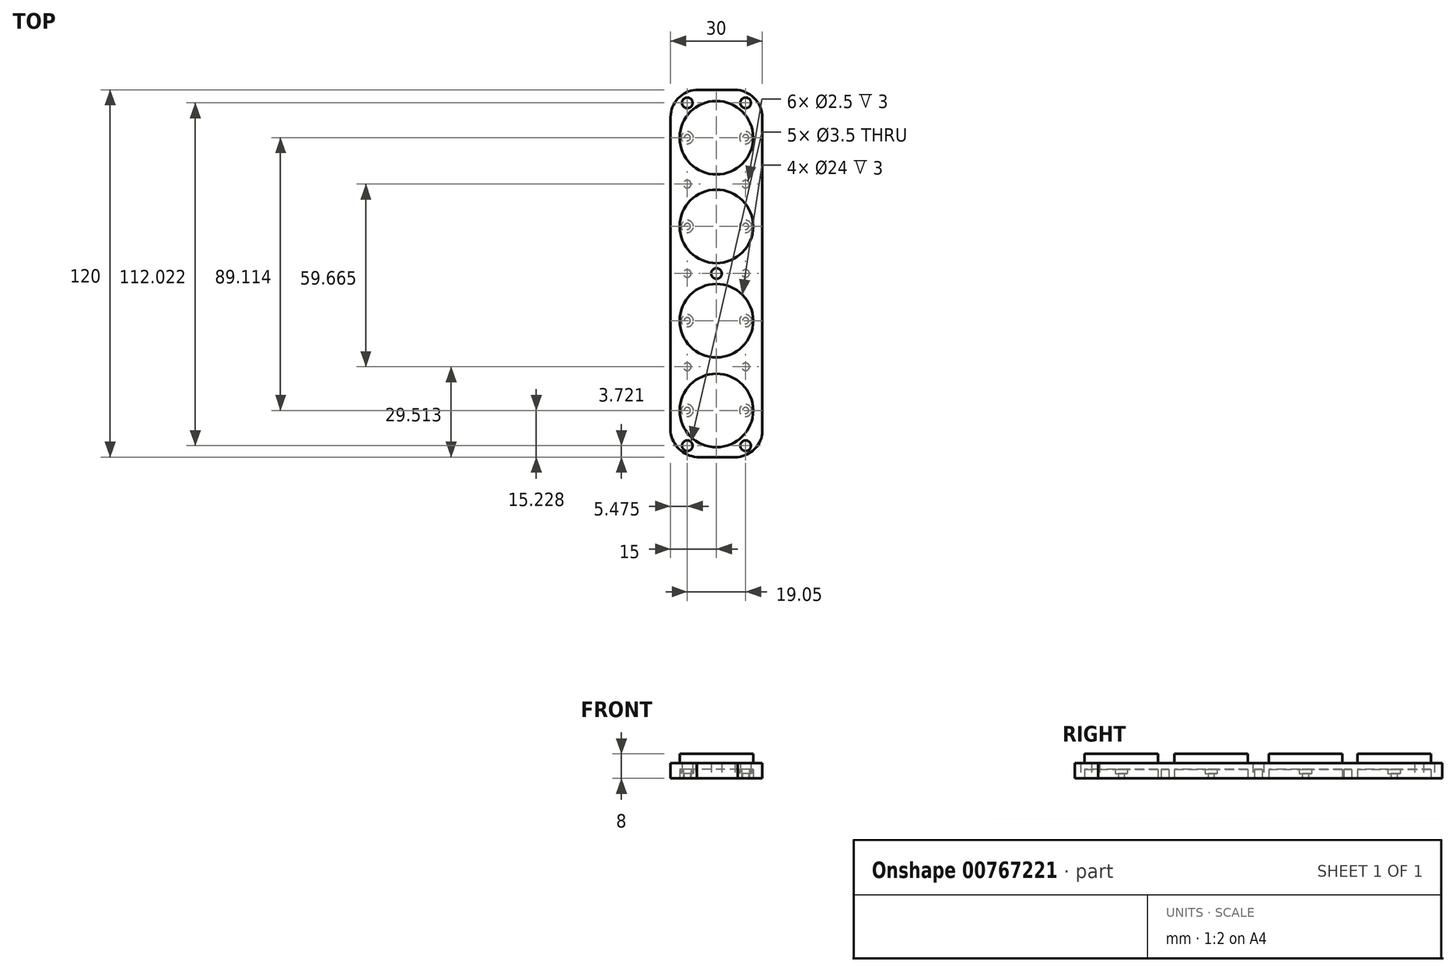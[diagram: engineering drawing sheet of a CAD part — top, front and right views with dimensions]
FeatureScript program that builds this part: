
annotation { "Feature Type Name" : "Feature", "Feature Type Description" : "" }
export const myFeature = defineFeature(function(context is Context, id is Id, definition is map)
    precondition{}
    {
        {
            var Q0;
            Q0=qCreatedBy(makeId("Top.planeOp"),FACE);
            var sketch = newSketch(context, id + "F0", { "sketchPlane" : qUnion([Q0])});
            skLineSegment(sketch, "E0.bottom", {"start": v(-15, 60.02) * mm, "end": v(15, 60.02) * mm});
            skLineSegment(sketch, "E0.top", {"start": v(-15, -59.98) * mm, "end": v(15, -59.98) * mm});
            skLineSegment(sketch, "E0.left", {"start": v(-15, 60.02) * mm, "end": v(-15, -59.98) * mm});
            skLineSegment(sketch, "E0.right", {"start": v(15, 60.02) * mm, "end": v(15, -59.98) * mm});
            skCircle(sketch, "E1", {"center": v(0, 44.36) * mm, "radius": 12 * mm});
            skCircle(sketch, "E2", {"center": v(0, 15.4) * mm, "radius": 12 * mm});
            skCircle(sketch, "E3", {"center": v(0, -15.42) * mm, "radius": 12 * mm});
            skCircle(sketch, "E4", {"center": v(0, -44.75) * mm, "radius": 12 * mm});
            skArc(sketch, "E5", {"start": v(-15, -49.5) * mm, "mid": v(-12.48, -57.1) * mm, "end": v(-5, -59.98) * mm});
            skArc(sketch, "E6", {"start": v(5, -59.98) * mm, "mid": v(12.6, -57.22) * mm, "end": v(15, -49.5) * mm});
            skArc(sketch, "E7", {"start": v(15, 50.8) * mm, "mid": v(12.4, 57.26) * mm, "end": v(6, 60.02) * mm});
            skArc(sketch, "E8", {"start": v(-5, 60.02) * mm, "mid": v(-12.07, 57.65) * mm, "end": v(-15, 50.8) * mm});
            skLineSegment(sketch, "E9", {"start": v(9.53, 68.25) * mm, "end": v(9.53, -73.05) * mm, "construction": true});
            skLineSegment(sketch, "E10", {"start": v(-9.53, 68.25) * mm, "end": v(-9.53, -73.05) * mm, "construction": true});
            skCircle(sketch, "E11", {"center": v(-9.53, 44.36) * mm, "radius": 1 * mm});
            skCircle(sketch, "E12", {"center": v(9.53, 44.36) * mm, "radius": 1 * mm});
            skCircle(sketch, "E13", {"center": v(9.53, 44.36) * mm, "radius": 2 * mm});
            skCircle(sketch, "E14", {"center": v(-9.53, 44.36) * mm, "radius": 2 * mm});
            skCircle(sketch, "E15", {"center": v(9.53, 15.4) * mm, "radius": 1 * mm});
            skCircle(sketch, "E16", {"center": v(9.53, 15.4) * mm, "radius": 2 * mm});
            skCircle(sketch, "E17", {"center": v(-9.53, 15.4) * mm, "radius": 1 * mm});
            skCircle(sketch, "E18", {"center": v(-9.53, 15.4) * mm, "radius": 2 * mm});
            skCircle(sketch, "E19", {"center": v(9.53, -15.42) * mm, "radius": 1 * mm});
            skCircle(sketch, "E20", {"center": v(9.53, -15.42) * mm, "radius": 2 * mm});
            skCircle(sketch, "E21", {"center": v(-9.53, -15.42) * mm, "radius": 1 * mm});
            skCircle(sketch, "E22", {"center": v(-9.53, -15.42) * mm, "radius": 2 * mm});
            skCircle(sketch, "E23", {"center": v(9.53, -44.75) * mm, "radius": 1 * mm});
            skCircle(sketch, "E24", {"center": v(9.53, -44.75) * mm, "radius": 2 * mm});
            skCircle(sketch, "E25", {"center": v(-9.53, -44.75) * mm, "radius": 1 * mm});
            skCircle(sketch, "E26", {"center": v(-9.53, -44.75) * mm, "radius": 2 * mm});
            skCircle(sketch, "E27", {"center": v(9.53, 55.76) * mm, "radius": 1.75 * mm});
            skCircle(sketch, "E28", {"center": v(-9.53, 55.76) * mm, "radius": 1.75 * mm});
            skCircle(sketch, "E29", {"center": v(9.53, 29.2) * mm, "radius": 1.25 * mm});
            skCircle(sketch, "E30", {"center": v(-9.53, 29.2) * mm, "radius": 1.25 * mm});
            skCircle(sketch, "E31", {"center": v(9.53, 0) * mm, "radius": 1.25 * mm});
            skCircle(sketch, "E32", {"center": v(-9.53, 0) * mm, "radius": 1.25 * mm});
            skCircle(sketch, "E33", {"center": v(9.53, -30.47) * mm, "radius": 1.25 * mm});
            skCircle(sketch, "E34", {"center": v(-9.53, -30.47) * mm, "radius": 1.25 * mm});
            skCircle(sketch, "E35", {"center": v(9.53, -56.26) * mm, "radius": 1.75 * mm});
            skCircle(sketch, "E36", {"center": v(-9.53, -56.26) * mm, "radius": 1.75 * mm});
            skCircle(sketch, "E37", {"center": v(0, 0) * mm, "radius": 1.75 * mm});
            skSolve(sketch);
        }
        {
            var Q0;
            Q0=makeQuery(id+"F0.imprint","IMPRINT",FACE,{"disambiguationData":[TD([[makeQuery(id+"F0.imprint","IMPRINT",EDGE,{"derivedFrom":sQuery(id+"F0.wireOp",EDGE,"E1")}),-1.0]])]});
            extrude(context, id + "F1", {"entities" : qUnion([Q0]), "depth" : 5 * mm, "offsetDistance" : 25 * mm});
        }
        {
            var Q0;
            Q0=makeQuery(id+"F0.imprint","IMPRINT",FACE,{"disambiguationData":[TD([[makeQuery(id+"F0.imprint","IMPRINT",EDGE,{"derivedFrom":sQuery(id+"F0.wireOp",EDGE,"E1")}),1.0]])]});
            var Q1;
            Q1=makeQuery(id+"F0.imprint","IMPRINT",FACE,{"disambiguationData":[TD([[makeQuery(id+"F0.imprint","IMPRINT",EDGE,{"derivedFrom":sQuery(id+"F0.wireOp",EDGE,"E2")}),1.0]])]});
            var Q2;
            Q2=makeQuery(id+"F0.imprint","IMPRINT",FACE,{"disambiguationData":[TD([[makeQuery(id+"F0.imprint","IMPRINT",EDGE,{"derivedFrom":sQuery(id+"F0.wireOp",EDGE,"E3")}),1.0]])]});
            var Q3;
            Q3=makeQuery(id+"F0.imprint","IMPRINT",FACE,{"disambiguationData":[TD([[makeQuery(id+"F0.imprint","IMPRINT",EDGE,{"derivedFrom":sQuery(id+"F0.wireOp",EDGE,"E4")}),1.0]])]});
            var Q4;
            Q4=makeQuery(id+"F0.imprint","IMPRINT",FACE,{"disambiguationData":[TD([[makeQuery(id+"F0.imprint","IMPRINT",EDGE,{"derivedFrom":sQuery(id+"F0.wireOp",EDGE,"E12")}),1.0]])]});
            var Q5;
            Q5=makeQuery(id+"F0.imprint","IMPRINT",FACE,{"disambiguationData":[TD([[makeQuery(id+"F0.imprint","IMPRINT",EDGE,{"derivedFrom":sQuery(id+"F0.wireOp",EDGE,"E12")}),-1.0]])]});
            var Q6;
            Q6=makeQuery(id+"F0.imprint","IMPRINT",FACE,{"disambiguationData":[TD([[makeQuery(id+"F0.imprint","IMPRINT",EDGE,{"derivedFrom":sQuery(id+"F0.wireOp",EDGE,"E11")}),1.0]])]});
            var Q7;
            Q7=makeQuery(id+"F0.imprint","IMPRINT",FACE,{"disambiguationData":[TD([[makeQuery(id+"F0.imprint","IMPRINT",EDGE,{"derivedFrom":sQuery(id+"F0.wireOp",EDGE,"E11")}),-1.0]])]});
            var Q8;
            Q8=makeQuery(id+"F0.imprint","IMPRINT",FACE,{"disambiguationData":[TD([[makeQuery(id+"F0.imprint","IMPRINT",EDGE,{"derivedFrom":sQuery(id+"F0.wireOp",EDGE,"E15")}),1.0]])]});
            var Q9;
            Q9=makeQuery(id+"F0.imprint","IMPRINT",FACE,{"disambiguationData":[TD([[makeQuery(id+"F0.imprint","IMPRINT",EDGE,{"derivedFrom":sQuery(id+"F0.wireOp",EDGE,"E15")}),-1.0]])]});
            var Q10;
            Q10=makeQuery(id+"F0.imprint","IMPRINT",FACE,{"disambiguationData":[TD([[makeQuery(id+"F0.imprint","IMPRINT",EDGE,{"derivedFrom":sQuery(id+"F0.wireOp",EDGE,"E17")}),1.0]])]});
            var Q11;
            Q11=makeQuery(id+"F0.imprint","IMPRINT",FACE,{"disambiguationData":[TD([[makeQuery(id+"F0.imprint","IMPRINT",EDGE,{"derivedFrom":sQuery(id+"F0.wireOp",EDGE,"E17")}),-1.0]])]});
            var Q12;
            Q12=makeQuery(id+"F0.imprint","IMPRINT",FACE,{"disambiguationData":[TD([[makeQuery(id+"F0.imprint","IMPRINT",EDGE,{"derivedFrom":sQuery(id+"F0.wireOp",EDGE,"E19")}),1.0]])]});
            var Q13;
            Q13=makeQuery(id+"F0.imprint","IMPRINT",FACE,{"disambiguationData":[TD([[makeQuery(id+"F0.imprint","IMPRINT",EDGE,{"derivedFrom":sQuery(id+"F0.wireOp",EDGE,"E19")}),-1.0]])]});
            var Q14;
            Q14=makeQuery(id+"F0.imprint","IMPRINT",FACE,{"disambiguationData":[TD([[makeQuery(id+"F0.imprint","IMPRINT",EDGE,{"derivedFrom":sQuery(id+"F0.wireOp",EDGE,"E21")}),1.0]])]});
            var Q15;
            Q15=makeQuery(id+"F0.imprint","IMPRINT",FACE,{"disambiguationData":[TD([[makeQuery(id+"F0.imprint","IMPRINT",EDGE,{"derivedFrom":sQuery(id+"F0.wireOp",EDGE,"E21")}),-1.0]])]});
            var Q16;
            Q16=makeQuery(id+"F0.imprint","IMPRINT",FACE,{"disambiguationData":[TD([[makeQuery(id+"F0.imprint","IMPRINT",EDGE,{"derivedFrom":sQuery(id+"F0.wireOp",EDGE,"E23")}),1.0]])]});
            var Q17;
            Q17=makeQuery(id+"F0.imprint","IMPRINT",FACE,{"disambiguationData":[TD([[makeQuery(id+"F0.imprint","IMPRINT",EDGE,{"derivedFrom":sQuery(id+"F0.wireOp",EDGE,"E23")}),-1.0]])]});
            var Q18;
            Q18=makeQuery(id+"F0.imprint","IMPRINT",FACE,{"disambiguationData":[TD([[makeQuery(id+"F0.imprint","IMPRINT",EDGE,{"derivedFrom":sQuery(id+"F0.wireOp",EDGE,"E25")}),-1.0]])]});
            var Q19;
            Q19=makeQuery(id+"F0.imprint","IMPRINT",FACE,{"disambiguationData":[TD([[makeQuery(id+"F0.imprint","IMPRINT",EDGE,{"derivedFrom":sQuery(id+"F0.wireOp",EDGE,"E25")}),1.0]])]});
            var Q20;
            Q20=makeQuery(id+"F0.imprint","IMPRINT",FACE,{"disambiguationData":[TD([[makeQuery(id+"F0.imprint","IMPRINT",EDGE,{"derivedFrom":sQuery(id+"F0.wireOp",EDGE,"E34")}),1.0]])]});
            var Q21;
            Q21=makeQuery(id+"F0.imprint","IMPRINT",FACE,{"disambiguationData":[TD([[makeQuery(id+"F0.imprint","IMPRINT",EDGE,{"derivedFrom":sQuery(id+"F0.wireOp",EDGE,"E33")}),1.0]])]});
            var Q22;
            Q22=makeQuery(id+"F0.imprint","IMPRINT",FACE,{"disambiguationData":[TD([[makeQuery(id+"F0.imprint","IMPRINT",EDGE,{"derivedFrom":sQuery(id+"F0.wireOp",EDGE,"E31")}),1.0]])]});
            var Q23;
            Q23=makeQuery(id+"F0.imprint","IMPRINT",FACE,{"disambiguationData":[TD([[makeQuery(id+"F0.imprint","IMPRINT",EDGE,{"derivedFrom":sQuery(id+"F0.wireOp",EDGE,"E32")}),1.0]])]});
            var Q24;
            Q24=makeQuery(id+"F0.imprint","IMPRINT",FACE,{"disambiguationData":[TD([[makeQuery(id+"F0.imprint","IMPRINT",EDGE,{"derivedFrom":sQuery(id+"F0.wireOp",EDGE,"E30")}),1.0]])]});
            var Q25;
            Q25=makeQuery(id+"F0.imprint","IMPRINT",FACE,{"disambiguationData":[TD([[makeQuery(id+"F0.imprint","IMPRINT",EDGE,{"derivedFrom":sQuery(id+"F0.wireOp",EDGE,"E29")}),1.0]])]});
            extrude(context, id + "F2", {"entities" : qUnion([Q0, Q1, Q2, Q3, Q4, Q5, Q6, Q7, Q8, Q9, Q10, Q11, Q12, Q13, Q14, Q15, Q16, Q17, Q18, Q19, Q20, Q21, Q22, Q23, Q24, Q25]), "operationType" : NewBodyOperationType.ADD, "depth" : 5 * mm, "offsetDistance" : 25 * mm, "hasSecondDirection" : true, "secondDirectionOppositeDirection" : false, "secondDirectionDepth" : 3 * mm});
        }
        {
            var Q0;
            Q0=makeQuery(id+"F0.imprint","IMPRINT",FACE,{"disambiguationData":[TD([[makeQuery(id+"F0.imprint","IMPRINT",EDGE,{"derivedFrom":sQuery(id+"F0.wireOp",EDGE,"E12")}),1.0]])]});
            var Q1;
            Q1=makeQuery(id+"F0.imprint","IMPRINT",FACE,{"disambiguationData":[TD([[makeQuery(id+"F0.imprint","IMPRINT",EDGE,{"derivedFrom":sQuery(id+"F0.wireOp",EDGE,"E11")}),1.0]])]});
            var Q2;
            Q2=makeQuery(id+"F0.imprint","IMPRINT",FACE,{"disambiguationData":[TD([[makeQuery(id+"F0.imprint","IMPRINT",EDGE,{"derivedFrom":sQuery(id+"F0.wireOp",EDGE,"E15")}),1.0]])]});
            var Q3;
            Q3=makeQuery(id+"F0.imprint","IMPRINT",FACE,{"disambiguationData":[TD([[makeQuery(id+"F0.imprint","IMPRINT",EDGE,{"derivedFrom":sQuery(id+"F0.wireOp",EDGE,"E17")}),1.0]])]});
            var Q4;
            Q4=makeQuery(id+"F0.imprint","IMPRINT",FACE,{"disambiguationData":[TD([[makeQuery(id+"F0.imprint","IMPRINT",EDGE,{"derivedFrom":sQuery(id+"F0.wireOp",EDGE,"E19")}),1.0]])]});
            var Q5;
            Q5=makeQuery(id+"F0.imprint","IMPRINT",FACE,{"disambiguationData":[TD([[makeQuery(id+"F0.imprint","IMPRINT",EDGE,{"derivedFrom":sQuery(id+"F0.wireOp",EDGE,"E21")}),1.0]])]});
            var Q6;
            Q6=makeQuery(id+"F0.imprint","IMPRINT",FACE,{"disambiguationData":[TD([[makeQuery(id+"F0.imprint","IMPRINT",EDGE,{"derivedFrom":sQuery(id+"F0.wireOp",EDGE,"E23")}),1.0]])]});
            var Q7;
            Q7=makeQuery(id+"F0.imprint","IMPRINT",FACE,{"disambiguationData":[TD([[makeQuery(id+"F0.imprint","IMPRINT",EDGE,{"derivedFrom":sQuery(id+"F0.wireOp",EDGE,"E25")}),1.0]])]});
            extrude(context, id + "F3", {"entities" : qUnion([Q0, Q1, Q2, Q3, Q4, Q5, Q6, Q7]), "operationType" : NewBodyOperationType.ADD, "depth" : 5 * mm, "offsetDistance" : 25 * mm, "hasSecondDirection" : true, "secondDirectionOppositeDirection" : true, "secondDirectionDepth" : 0 * mm});
        }
        {
            var Q0;
            Q0=makeQuery(id+"F0.imprint","IMPRINT",FACE,{"disambiguationData":[TD([[makeQuery(id+"F0.imprint","IMPRINT",EDGE,{"derivedFrom":sQuery(id+"F0.wireOp",EDGE,"E12")}),-1.0]])]});
            var Q1;
            Q1=makeQuery(id+"F0.imprint","IMPRINT",FACE,{"disambiguationData":[TD([[makeQuery(id+"F0.imprint","IMPRINT",EDGE,{"derivedFrom":sQuery(id+"F0.wireOp",EDGE,"E11")}),-1.0]])]});
            var Q2;
            Q2=makeQuery(id+"F0.imprint","IMPRINT",FACE,{"disambiguationData":[TD([[makeQuery(id+"F0.imprint","IMPRINT",EDGE,{"derivedFrom":sQuery(id+"F0.wireOp",EDGE,"E15")}),-1.0]])]});
            var Q3;
            Q3=makeQuery(id+"F0.imprint","IMPRINT",FACE,{"disambiguationData":[TD([[makeQuery(id+"F0.imprint","IMPRINT",EDGE,{"derivedFrom":sQuery(id+"F0.wireOp",EDGE,"E17")}),-1.0]])]});
            var Q4;
            Q4=makeQuery(id+"F0.imprint","IMPRINT",FACE,{"disambiguationData":[TD([[makeQuery(id+"F0.imprint","IMPRINT",EDGE,{"derivedFrom":sQuery(id+"F0.wireOp",EDGE,"E19")}),-1.0]])]});
            var Q5;
            Q5=makeQuery(id+"F0.imprint","IMPRINT",FACE,{"disambiguationData":[TD([[makeQuery(id+"F0.imprint","IMPRINT",EDGE,{"derivedFrom":sQuery(id+"F0.wireOp",EDGE,"E21")}),-1.0]])]});
            var Q6;
            Q6=makeQuery(id+"F0.imprint","IMPRINT",FACE,{"disambiguationData":[TD([[makeQuery(id+"F0.imprint","IMPRINT",EDGE,{"derivedFrom":sQuery(id+"F0.wireOp",EDGE,"E23")}),-1.0]])]});
            var Q7;
            Q7=makeQuery(id+"F0.imprint","IMPRINT",FACE,{"disambiguationData":[TD([[makeQuery(id+"F0.imprint","IMPRINT",EDGE,{"derivedFrom":sQuery(id+"F0.wireOp",EDGE,"E25")}),-1.0]])]});
            extrude(context, id + "F4", {"entities" : qUnion([Q0, Q1, Q2, Q3, Q4, Q5, Q6, Q7]), "operationType" : NewBodyOperationType.ADD, "depth" : 5 * mm, "offsetDistance" : 25 * mm, "hasSecondDirection" : true, "secondDirectionOppositeDirection" : false, "secondDirectionDepth" : 1.6 * mm});
        }
        {
            var Q0;
            Q0=makeQuery(id+"F0.imprint","IMPRINT",FACE,{"disambiguationData":[TD([[makeQuery(id+"F0.imprint","IMPRINT",EDGE,{"derivedFrom":sQuery(id+"F0.wireOp",EDGE,"E35")}),1.0]])]});
            var Q1;
            Q1=makeQuery(id+"F0.imprint","IMPRINT",FACE,{"disambiguationData":[TD([[makeQuery(id+"F0.imprint","IMPRINT",EDGE,{"derivedFrom":sQuery(id+"F0.wireOp",EDGE,"E36")}),1.0]])]});
            var Q2;
            Q2=makeQuery(id+"F0.imprint","IMPRINT",FACE,{"disambiguationData":[TD([[makeQuery(id+"F0.imprint","IMPRINT",EDGE,{"derivedFrom":sQuery(id+"F0.wireOp",EDGE,"E34")}),1.0]])]});
            var Q3;
            Q3=makeQuery(id+"F0.imprint","IMPRINT",FACE,{"disambiguationData":[TD([[makeQuery(id+"F0.imprint","IMPRINT",EDGE,{"derivedFrom":sQuery(id+"F0.wireOp",EDGE,"E33")}),1.0]])]});
            var Q4;
            Q4=makeQuery(id+"F0.imprint","IMPRINT",FACE,{"disambiguationData":[TD([[makeQuery(id+"F0.imprint","IMPRINT",EDGE,{"derivedFrom":sQuery(id+"F0.wireOp",EDGE,"E31")}),1.0]])]});
            var Q5;
            Q5=makeQuery(id+"F0.imprint","IMPRINT",FACE,{"disambiguationData":[TD([[makeQuery(id+"F0.imprint","IMPRINT",EDGE,{"derivedFrom":sQuery(id+"F0.wireOp",EDGE,"E32")}),1.0]])]});
            var Q6;
            Q6=makeQuery(id+"F0.imprint","IMPRINT",FACE,{"disambiguationData":[TD([[makeQuery(id+"F0.imprint","IMPRINT",EDGE,{"derivedFrom":sQuery(id+"F0.wireOp",EDGE,"E29")}),1.0]])]});
            var Q7;
            Q7=makeQuery(id+"F0.imprint","IMPRINT",FACE,{"disambiguationData":[TD([[makeQuery(id+"F0.imprint","IMPRINT",EDGE,{"derivedFrom":sQuery(id+"F0.wireOp",EDGE,"E30")}),1.0]])]});
            var Q8;
            Q8=makeQuery(id+"F0.imprint","IMPRINT",FACE,{"disambiguationData":[TD([[makeQuery(id+"F0.imprint","IMPRINT",EDGE,{"derivedFrom":sQuery(id+"F0.wireOp",EDGE,"E27")}),1.0]])]});
            var Q9;
            Q9=makeQuery(id+"F0.imprint","IMPRINT",FACE,{"disambiguationData":[TD([[makeQuery(id+"F0.imprint","IMPRINT",EDGE,{"derivedFrom":sQuery(id+"F0.wireOp",EDGE,"E28")}),1.0]])]});
            extrude(context, id + "F5", {"entities" : qUnion([Q0, Q1, Q2, Q3, Q4, Q5, Q6, Q7, Q8, Q9]), "operationType" : NewBodyOperationType.REMOVE, "depth" : 1.3 * mm, "offsetDistance" : 25 * mm, "hasSecondDirection" : true, "secondDirectionOppositeDirection" : true, "secondDirectionDepth" : 0.1 * mm});
        }
        {
            var Q0;
            Q0=makeQuery(id+"F0.imprint","IMPRINT",FACE,{"disambiguationData":[TD([[makeQuery(id+"F0.imprint","IMPRINT",EDGE,{"derivedFrom":sQuery(id+"F0.wireOp",EDGE,"E1")}),1.0]])]});
            var Q1;
            Q1=makeQuery(id+"F0.imprint","IMPRINT",FACE,{"disambiguationData":[TD([[makeQuery(id+"F0.imprint","IMPRINT",EDGE,{"derivedFrom":sQuery(id+"F0.wireOp",EDGE,"E2")}),1.0]])]});
            var Q2;
            Q2=makeQuery(id+"F0.imprint","IMPRINT",FACE,{"disambiguationData":[TD([[makeQuery(id+"F0.imprint","IMPRINT",EDGE,{"derivedFrom":sQuery(id+"F0.wireOp",EDGE,"E3")}),1.0]])]});
            var Q3;
            Q3=makeQuery(id+"F0.imprint","IMPRINT",FACE,{"disambiguationData":[TD([[makeQuery(id+"F0.imprint","IMPRINT",EDGE,{"derivedFrom":sQuery(id+"F0.wireOp",EDGE,"E4")}),1.0]])]});
            var Q4;
            Q4=makeQuery(id+"F0.imprint","IMPRINT",FACE,{"disambiguationData":[TD([[makeQuery(id+"F0.imprint","IMPRINT",EDGE,{"derivedFrom":sQuery(id+"F0.wireOp",EDGE,"E25")}),-1.0]])]});
            var Q5;
            Q5=makeQuery(id+"F0.imprint","IMPRINT",FACE,{"disambiguationData":[TD([[makeQuery(id+"F0.imprint","IMPRINT",EDGE,{"derivedFrom":sQuery(id+"F0.wireOp",EDGE,"E25")}),1.0]])]});
            var Q6;
            Q6=makeQuery(id+"F0.imprint","IMPRINT",FACE,{"disambiguationData":[TD([[makeQuery(id+"F0.imprint","IMPRINT",EDGE,{"derivedFrom":sQuery(id+"F0.wireOp",EDGE,"E23")}),1.0]])]});
            var Q7;
            Q7=makeQuery(id+"F0.imprint","IMPRINT",FACE,{"disambiguationData":[TD([[makeQuery(id+"F0.imprint","IMPRINT",EDGE,{"derivedFrom":sQuery(id+"F0.wireOp",EDGE,"E23")}),-1.0]])]});
            var Q8;
            Q8=makeQuery(id+"F0.imprint","IMPRINT",FACE,{"disambiguationData":[TD([[makeQuery(id+"F0.imprint","IMPRINT",EDGE,{"derivedFrom":sQuery(id+"F0.wireOp",EDGE,"E21")}),1.0]])]});
            var Q9;
            Q9=makeQuery(id+"F0.imprint","IMPRINT",FACE,{"disambiguationData":[TD([[makeQuery(id+"F0.imprint","IMPRINT",EDGE,{"derivedFrom":sQuery(id+"F0.wireOp",EDGE,"E21")}),-1.0]])]});
            var Q10;
            Q10=makeQuery(id+"F0.imprint","IMPRINT",FACE,{"disambiguationData":[TD([[makeQuery(id+"F0.imprint","IMPRINT",EDGE,{"derivedFrom":sQuery(id+"F0.wireOp",EDGE,"E19")}),-1.0]])]});
            var Q11;
            Q11=makeQuery(id+"F0.imprint","IMPRINT",FACE,{"disambiguationData":[TD([[makeQuery(id+"F0.imprint","IMPRINT",EDGE,{"derivedFrom":sQuery(id+"F0.wireOp",EDGE,"E19")}),1.0]])]});
            var Q12;
            Q12=makeQuery(id+"F0.imprint","IMPRINT",FACE,{"disambiguationData":[TD([[makeQuery(id+"F0.imprint","IMPRINT",EDGE,{"derivedFrom":sQuery(id+"F0.wireOp",EDGE,"E17")}),1.0]])]});
            var Q13;
            Q13=makeQuery(id+"F0.imprint","IMPRINT",FACE,{"disambiguationData":[TD([[makeQuery(id+"F0.imprint","IMPRINT",EDGE,{"derivedFrom":sQuery(id+"F0.wireOp",EDGE,"E17")}),-1.0]])]});
            var Q14;
            Q14=makeQuery(id+"F0.imprint","IMPRINT",FACE,{"disambiguationData":[TD([[makeQuery(id+"F0.imprint","IMPRINT",EDGE,{"derivedFrom":sQuery(id+"F0.wireOp",EDGE,"E15")}),-1.0]])]});
            var Q15;
            Q15=makeQuery(id+"F0.imprint","IMPRINT",FACE,{"disambiguationData":[TD([[makeQuery(id+"F0.imprint","IMPRINT",EDGE,{"derivedFrom":sQuery(id+"F0.wireOp",EDGE,"E15")}),1.0]])]});
            var Q16;
            Q16=makeQuery(id+"F0.imprint","IMPRINT",FACE,{"disambiguationData":[TD([[makeQuery(id+"F0.imprint","IMPRINT",EDGE,{"derivedFrom":sQuery(id+"F0.wireOp",EDGE,"E11")}),1.0]])]});
            var Q17;
            Q17=makeQuery(id+"F0.imprint","IMPRINT",FACE,{"disambiguationData":[TD([[makeQuery(id+"F0.imprint","IMPRINT",EDGE,{"derivedFrom":sQuery(id+"F0.wireOp",EDGE,"E11")}),-1.0]])]});
            var Q18;
            Q18=makeQuery(id+"F0.imprint","IMPRINT",FACE,{"disambiguationData":[TD([[makeQuery(id+"F0.imprint","IMPRINT",EDGE,{"derivedFrom":sQuery(id+"F0.wireOp",EDGE,"E12")}),-1.0]])]});
            var Q19;
            Q19=makeQuery(id+"F0.imprint","IMPRINT",FACE,{"disambiguationData":[TD([[makeQuery(id+"F0.imprint","IMPRINT",EDGE,{"derivedFrom":sQuery(id+"F0.wireOp",EDGE,"E12")}),1.0]])]});
            extrude(context, id + "F6", {"entities" : qUnion([Q0, Q1, Q2, Q3, Q4, Q5, Q6, Q7, Q8, Q9, Q10, Q11, Q12, Q13, Q14, Q15, Q16, Q17, Q18, Q19]), "operationType" : NewBodyOperationType.ADD, "depth" : 8 * mm, "offsetDistance" : 25 * mm, "hasSecondDirection" : true, "secondDirectionOppositeDirection" : false, "secondDirectionDepth" : 5 * mm});
        }
    });
